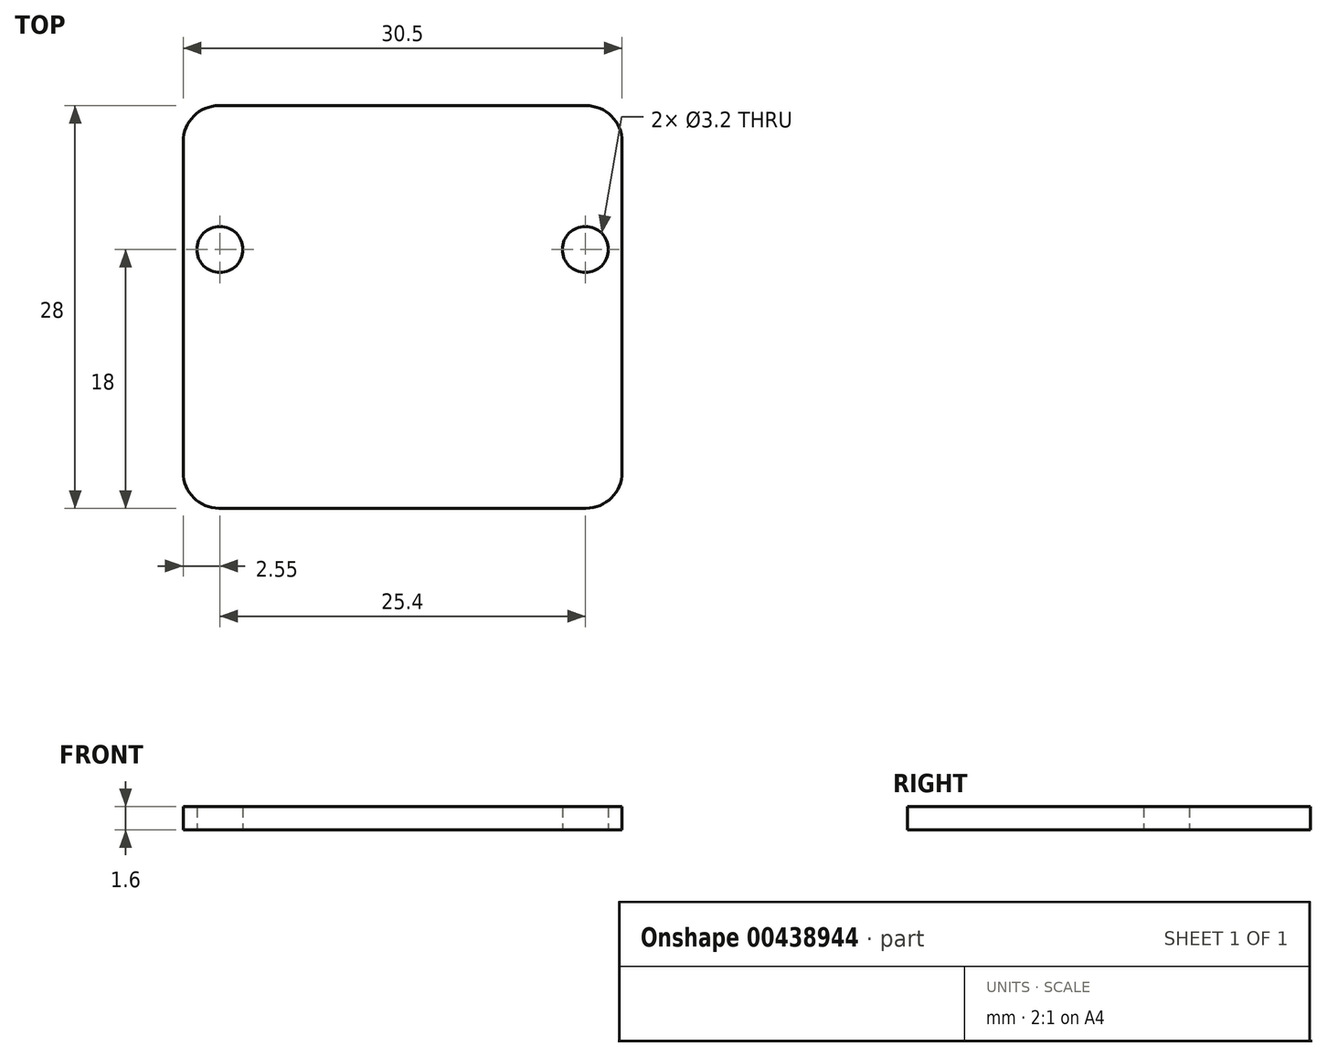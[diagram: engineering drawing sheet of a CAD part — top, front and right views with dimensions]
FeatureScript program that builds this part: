
annotation { "Feature Type Name" : "Feature", "Feature Type Description" : "" }
export const myFeature = defineFeature(function(context is Context, id is Id, definition is map)
    precondition{}
    {
        {
            var Q0;
            Q0=qCreatedBy(makeId("Top.planeOp"),FACE);
            var sketch = newSketch(context, id + "F0", { "sketchPlane" : qUnion([Q0])});
            skLineSegment(sketch, "E0.bottom", {"start": v(2.5, 0) * mm, "end": v(28, 0) * mm});
            skLineSegment(sketch, "E0.top", {"start": v(2.5, 28) * mm, "end": v(28, 28) * mm});
            skLineSegment(sketch, "E0.left", {"start": v(0, 2.5) * mm, "end": v(0, 25.5) * mm});
            skLineSegment(sketch, "E0.right", {"start": v(30.5, 2.5) * mm, "end": v(30.5, 25.5) * mm});
            skCircle(sketch, "E1", {"center": v(2.55, 18) * mm, "radius": 1.6 * mm});
            skCircle(sketch, "E2", {"center": v(27.95, 18) * mm, "radius": 1.6 * mm});
            skLineSegment(sketch, "E3", {"start": v(15.25, 28) * mm, "end": v(15.25, 0) * mm, "construction": true});
            skLineSegment(sketch, "E4", {"start": v(2.55, 18) * mm, "end": v(15.25, 18) * mm, "construction": true});
            skLineSegment(sketch, "E5", {"start": v(15.25, 18) * mm, "end": v(27.95, 18) * mm, "construction": true});
            skPoint(sketch, "E6.visualSharp", {"position": v(0, 28) * mm});
            skArc(sketch, "E6.filletArc", {"start": v(2.5, 28) * mm, "mid": v(0.73, 27.27) * mm, "end": v(0, 25.5) * mm});
            skPoint(sketch, "E7.visualSharp", {"position": v(30.5, 28) * mm});
            skArc(sketch, "E7.filletArc", {"start": v(30.5, 25.5) * mm, "mid": v(29.77, 27.27) * mm, "end": v(28, 28) * mm});
            skPoint(sketch, "E8.visualSharp", {"position": v(30.5, 0) * mm});
            skArc(sketch, "E8.filletArc", {"start": v(28, 0) * mm, "mid": v(29.77, 0.73) * mm, "end": v(30.5, 2.5) * mm});
            skPoint(sketch, "E9.visualSharp", {"position": v(0, 0) * mm});
            skArc(sketch, "E9.filletArc", {"start": v(0, 2.5) * mm, "mid": v(0.73, 0.73) * mm, "end": v(2.5, 0) * mm});
            skSolve(sketch);
        }
        {
            var Q0;
            Q0=makeQuery(id+"F0.imprint","IMPRINT",FACE,{"disambiguationData":[TD([[makeQuery(id+"F0.imprint","IMPRINT",EDGE,{"derivedFrom":sQuery(id+"F0.wireOp",EDGE,"E0.bottom")}),1.0]])]});
            extrude(context, id + "F1", {"entities" : qUnion([Q0]), "depth" : 1.6 * mm});
        }
    });
